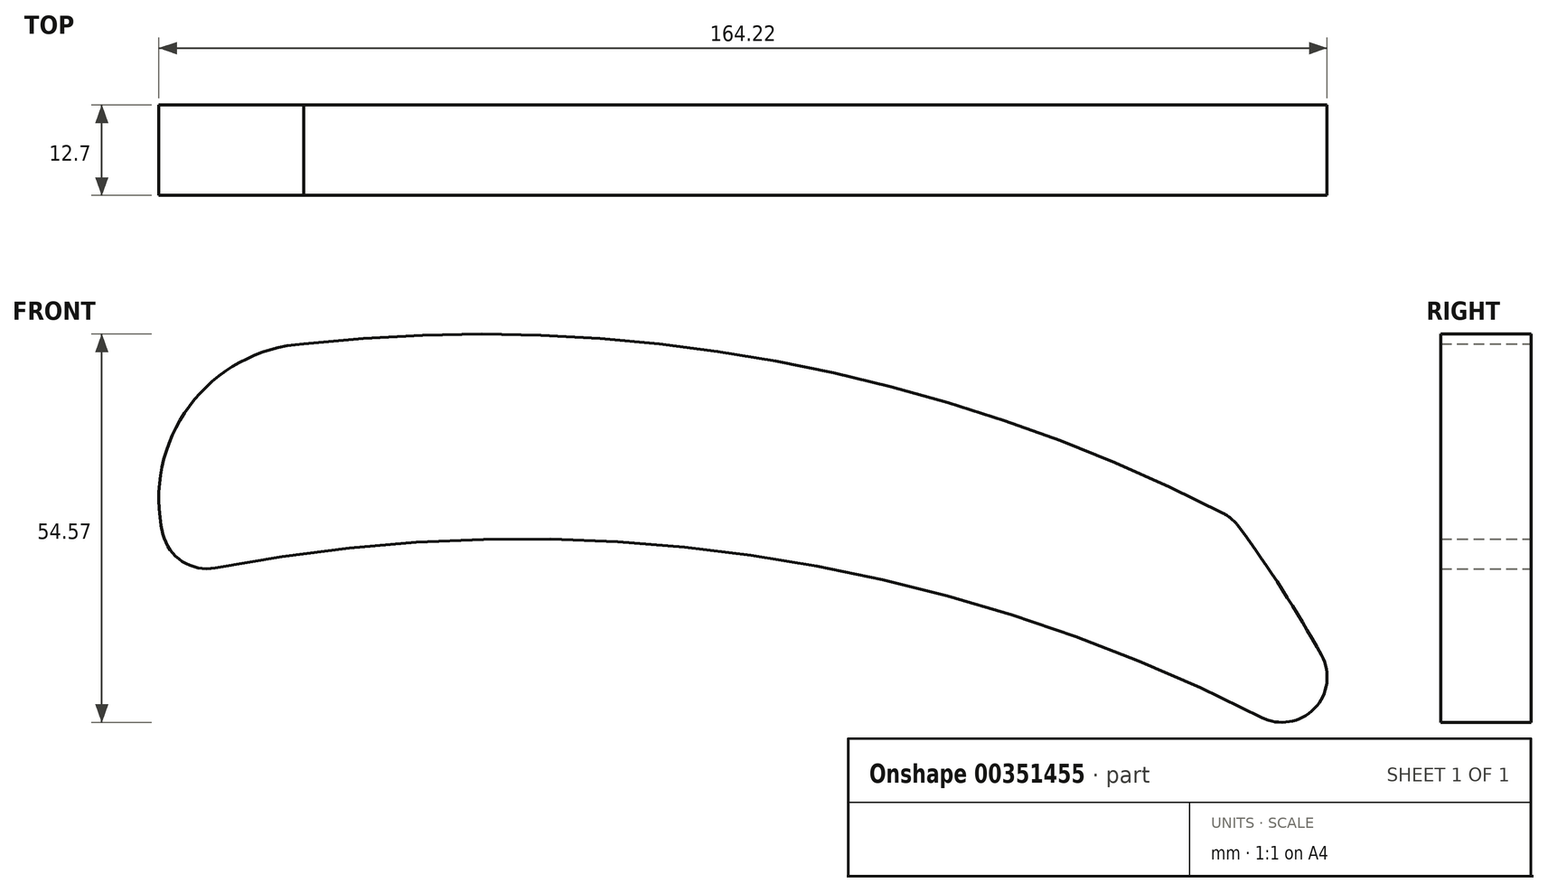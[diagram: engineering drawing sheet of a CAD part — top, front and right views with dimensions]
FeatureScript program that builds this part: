
annotation { "Feature Type Name" : "Feature", "Feature Type Description" : "" }
export const myFeature = defineFeature(function(context is Context, id is Id, definition is map)
    precondition{}
    {
        {
            var Q0;
            Q0=qCreatedBy(makeId("Front.planeOp"),FACE);
            var sketch = newSketch(context, id + "F0", { "sketchPlane" : qUnion([Q0])});
            skArc(sketch, "E0", {"start": v(-2.62, -9.47) * mm, "mid": v(-18.72, -18.24) * mm, "end": v(-22.43, -36.2) * mm});
            skArc(sketch, "E1", {"start": v(131.98, -61.98) * mm, "mid": v(60.22, -39.2) * mm, "end": v(-15.05, -40.98) * mm});
            skArc(sketch, "E2", {"start": v(126.6, -33.3) * mm, "mid": v(63.74, -11.9) * mm, "end": v(-2.62, -9.47) * mm});
            skArc(sketch, "E3", {"start": v(140.43, -53.25) * mm, "mid": v(134.92, -44.03) * mm, "end": v(128.82, -35.18) * mm});
            skPoint(sketch, "E4.visualSharp", {"position": v(127.93, -33.98) * mm});
            skArc(sketch, "E4.filletArc", {"start": v(128.82, -35.18) * mm, "mid": v(127.82, -34.1) * mm, "end": v(126.6, -33.3) * mm});
            skPoint(sketch, "E5.visualSharp", {"position": v(149.23, -71.77) * mm});
            skArc(sketch, "E5.filletArc", {"start": v(131.98, -61.98) * mm, "mid": v(139.44, -60.74) * mm, "end": v(140.43, -53.25) * mm});
            skPoint(sketch, "E6.visualSharp", {"position": v(-20.14, -42.01) * mm});
            skArc(sketch, "E6.filletArc", {"start": v(-22.43, -36.2) * mm, "mid": v(-19.7, -40.07) * mm, "end": v(-15.05, -40.98) * mm});
            skSolve(sketch);
        }
        {
            var Q0;
            Q0=makeQuery(id+"F0.imprint","IMPRINT",FACE,{"disambiguationData":[TD([[makeQuery(id+"F0.imprint","IMPRINT",EDGE,{"derivedFrom":sQuery(id+"F0.wireOp",EDGE,"E0")}),1.0]])]});
            extrude(context, id + "F1", {"entities" : qUnion([Q0]), "depth" : 12.7 * mm});
        }
    });
